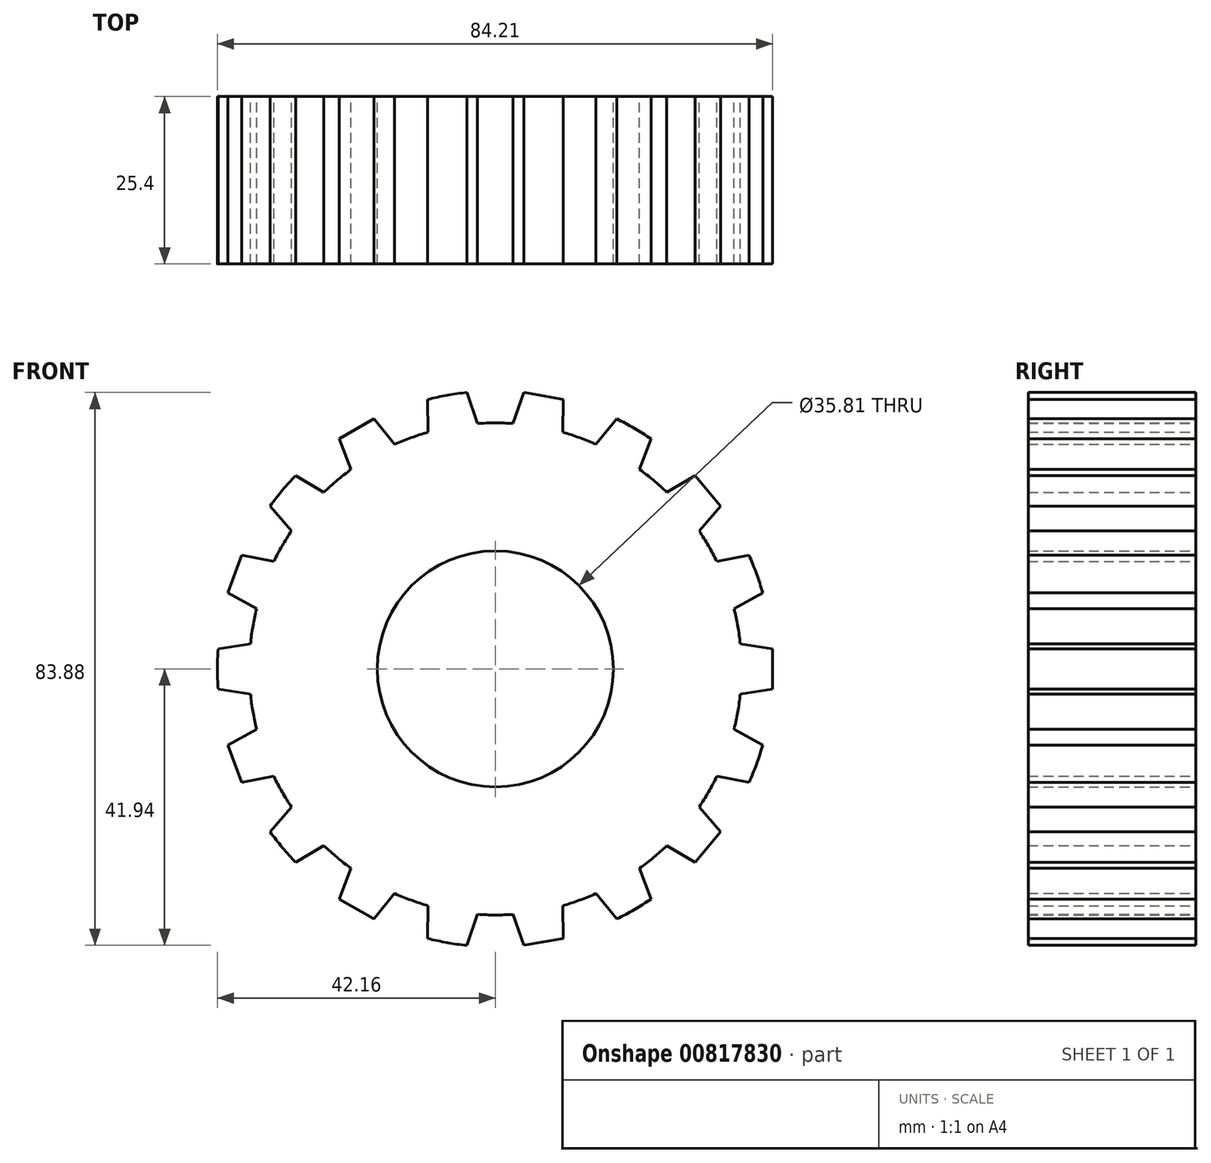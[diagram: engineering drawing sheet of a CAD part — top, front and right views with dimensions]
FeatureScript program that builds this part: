
annotation { "Feature Type Name" : "Feature", "Feature Type Description" : "" }
export const myFeature = defineFeature(function(context is Context, id is Id, definition is map)
    precondition{}
    {
        {
            var Q0;
            Q0=qCreatedBy(makeId("Front.planeOp"),FACE);
            var sketch = newSketch(context, id + "F0", { "sketchPlane" : qUnion([Q0])});
            skCircle(sketch, "E0", {"center": v(0, 0) * mm, "radius": 17.9 * mm});
            skArc(sketch, "E1", {"start": v(37.14, 3.81) * mm, "mid": v(36.77, 6.48) * mm, "end": v(36.2, 9.12) * mm});
            skArc(sketch, "E2", {"start": v(40.56, 11.53) * mm, "mid": v(39.62, 14.42) * mm, "end": v(38.48, 17.24) * mm});
            skLineSegment(sketch, "E3", {"start": v(42.16, 0) * mm, "end": v(61.21, 0) * mm});
            skLineSegment(sketch, "E4", {"start": v(42.05, 3.03) * mm, "end": v(37.14, 3.81) * mm});
            skLineSegment(sketch, "E5", {"start": v(42.05, -3.03) * mm, "end": v(37.14, -3.81) * mm});
            skLineSegment(sketch, "E6", {"start": v(42.05, 3.03) * mm, "end": v(42.05, -3.03) * mm});
            skLineSegment(sketch, "E7", {"start": v(36.2, 9.12) * mm, "end": v(40.56, 11.53) * mm});
            skLineSegment(sketch, "E8.MirrorCS", {"start": v(42.05, -3.03) * mm, "end": v(42.05, 3.03) * mm});
            skArc(sketch, "E9.MirrorCS", {"start": v(37.14, -3.81) * mm, "mid": v(36.77, -6.48) * mm, "end": v(36.2, -9.12) * mm});
            skLineSegment(sketch, "E10.MirrorCS", {"start": v(36.2, -9.12) * mm, "end": v(40.56, -11.53) * mm});
            skLineSegment(sketch, "E11.1.0", {"start": v(21.87, 30.26) * mm, "end": v(23.66, 34.9) * mm});
            skArc(sketch, "E11.1.1", {"start": v(26, 26.8) * mm, "mid": v(24, 28.6) * mm, "end": v(21.87, 30.26) * mm});
            skLineSegment(sketch, "E11.1.2", {"start": v(30.27, 29.36) * mm, "end": v(26, 26.8) * mm});
            skLineSegment(sketch, "E11.1.3", {"start": v(34.17, 24.7) * mm, "end": v(30.27, 29.36) * mm});
            skLineSegment(sketch, "E11.1.4", {"start": v(34.17, 24.7) * mm, "end": v(30.9, 20.95) * mm});
            skArc(sketch, "E11.1.5", {"start": v(30.9, 20.95) * mm, "mid": v(32.34, 18.67) * mm, "end": v(33.6, 16.29) * mm});
            skLineSegment(sketch, "E11.1.6", {"start": v(33.6, 16.29) * mm, "end": v(38.48, 17.24) * mm});
            skLineSegment(sketch, "E11.2.0", {"start": v(-2.7, 37.24) * mm, "end": v(-4.31, 41.94) * mm});
            skArc(sketch, "E11.2.1", {"start": v(2.7, 37.24) * mm, "mid": v(0, 37.34) * mm, "end": v(-2.7, 37.24) * mm});
            skLineSegment(sketch, "E11.2.2", {"start": v(4.31, 41.94) * mm, "end": v(2.7, 37.24) * mm});
            skLineSegment(sketch, "E11.2.3", {"start": v(10.3, 40.89) * mm, "end": v(4.31, 41.94) * mm});
            skLineSegment(sketch, "E11.2.4", {"start": v(10.3, 40.89) * mm, "end": v(10.2, 35.92) * mm});
            skArc(sketch, "E11.2.5", {"start": v(10.2, 35.92) * mm, "mid": v(12.77, 35.09) * mm, "end": v(15.27, 34.07) * mm});
            skLineSegment(sketch, "E11.2.6", {"start": v(15.27, 34.07) * mm, "end": v(18.4, 37.94) * mm});
            skLineSegment(sketch, "E11.3.0", {"start": v(-26, 26.8) * mm, "end": v(-30.27, 29.36) * mm});
            skArc(sketch, "E11.3.1", {"start": v(-21.87, 30.26) * mm, "mid": v(-24, 28.6) * mm, "end": v(-26, 26.8) * mm});
            skLineSegment(sketch, "E11.3.2", {"start": v(-23.66, 34.9) * mm, "end": v(-21.87, 30.26) * mm});
            skLineSegment(sketch, "E11.3.3", {"start": v(-18.4, 37.94) * mm, "end": v(-23.66, 34.9) * mm});
            skLineSegment(sketch, "E11.3.4", {"start": v(-18.4, 37.94) * mm, "end": v(-15.27, 34.07) * mm});
            skArc(sketch, "E11.3.5", {"start": v(-15.27, 34.07) * mm, "mid": v(-12.77, 35.09) * mm, "end": v(-10.2, 35.92) * mm});
            skLineSegment(sketch, "E11.3.6", {"start": v(-10.2, 35.92) * mm, "end": v(-10.3, 40.89) * mm});
            skLineSegment(sketch, "E11.4.0", {"start": v(-37.14, 3.81) * mm, "end": v(-42.05, 3.03) * mm});
            skArc(sketch, "E11.4.1", {"start": v(-36.2, 9.12) * mm, "mid": v(-36.77, 6.48) * mm, "end": v(-37.14, 3.81) * mm});
            skLineSegment(sketch, "E11.4.2", {"start": v(-40.56, 11.53) * mm, "end": v(-36.2, 9.12) * mm});
            skLineSegment(sketch, "E11.4.3", {"start": v(-38.48, 17.24) * mm, "end": v(-40.56, 11.53) * mm});
            skLineSegment(sketch, "E11.4.4", {"start": v(-38.48, 17.24) * mm, "end": v(-33.6, 16.29) * mm});
            skArc(sketch, "E11.4.5", {"start": v(-33.6, 16.29) * mm, "mid": v(-32.34, 18.67) * mm, "end": v(-30.9, 20.95) * mm});
            skLineSegment(sketch, "E11.4.6", {"start": v(-30.9, 20.95) * mm, "end": v(-34.17, 24.7) * mm});
            skLineSegment(sketch, "E11.5.0", {"start": v(-30.9, -20.95) * mm, "end": v(-34.17, -24.7) * mm});
            skArc(sketch, "E11.5.1", {"start": v(-33.6, -16.29) * mm, "mid": v(-32.34, -18.67) * mm, "end": v(-30.9, -20.95) * mm});
            skLineSegment(sketch, "E11.5.2", {"start": v(-38.48, -17.24) * mm, "end": v(-33.6, -16.29) * mm});
            skLineSegment(sketch, "E11.5.3", {"start": v(-40.56, -11.53) * mm, "end": v(-38.48, -17.24) * mm});
            skLineSegment(sketch, "E11.5.4", {"start": v(-40.56, -11.53) * mm, "end": v(-36.2, -9.12) * mm});
            skArc(sketch, "E11.5.5", {"start": v(-36.2, -9.12) * mm, "mid": v(-36.77, -6.48) * mm, "end": v(-37.14, -3.81) * mm});
            skLineSegment(sketch, "E11.5.6", {"start": v(-37.14, -3.81) * mm, "end": v(-42.05, -3.03) * mm});
            skLineSegment(sketch, "E11.6.0", {"start": v(-10.2, -35.92) * mm, "end": v(-10.3, -40.89) * mm});
            skArc(sketch, "E11.6.1", {"start": v(-15.27, -34.07) * mm, "mid": v(-12.77, -35.09) * mm, "end": v(-10.2, -35.92) * mm});
            skLineSegment(sketch, "E11.6.2", {"start": v(-18.4, -37.94) * mm, "end": v(-15.27, -34.07) * mm});
            skLineSegment(sketch, "E11.6.3", {"start": v(-23.66, -34.9) * mm, "end": v(-18.4, -37.94) * mm});
            skLineSegment(sketch, "E11.6.4", {"start": v(-23.66, -34.9) * mm, "end": v(-21.87, -30.26) * mm});
            skArc(sketch, "E11.6.5", {"start": v(-21.87, -30.26) * mm, "mid": v(-24, -28.6) * mm, "end": v(-26, -26.8) * mm});
            skLineSegment(sketch, "E11.6.6", {"start": v(-26, -26.8) * mm, "end": v(-30.27, -29.36) * mm});
            skLineSegment(sketch, "E11.7.0", {"start": v(15.27, -34.07) * mm, "end": v(18.4, -37.94) * mm});
            skArc(sketch, "E11.7.1", {"start": v(10.2, -35.92) * mm, "mid": v(12.77, -35.09) * mm, "end": v(15.27, -34.07) * mm});
            skLineSegment(sketch, "E11.7.2", {"start": v(10.3, -40.89) * mm, "end": v(10.2, -35.92) * mm});
            skLineSegment(sketch, "E11.7.3", {"start": v(4.31, -41.94) * mm, "end": v(10.3, -40.89) * mm});
            skLineSegment(sketch, "E11.7.4", {"start": v(4.31, -41.94) * mm, "end": v(2.7, -37.24) * mm});
            skArc(sketch, "E11.7.5", {"start": v(2.7, -37.24) * mm, "mid": v(0, -37.34) * mm, "end": v(-2.7, -37.24) * mm});
            skLineSegment(sketch, "E11.7.6", {"start": v(-2.7, -37.24) * mm, "end": v(-4.31, -41.94) * mm});
            skLineSegment(sketch, "E11.8.0", {"start": v(33.6, -16.29) * mm, "end": v(38.48, -17.24) * mm});
            skArc(sketch, "E11.8.1", {"start": v(30.9, -20.95) * mm, "mid": v(32.34, -18.67) * mm, "end": v(33.6, -16.29) * mm});
            skLineSegment(sketch, "E11.8.2", {"start": v(34.17, -24.7) * mm, "end": v(30.9, -20.95) * mm});
            skLineSegment(sketch, "E11.8.3", {"start": v(30.27, -29.36) * mm, "end": v(34.17, -24.7) * mm});
            skLineSegment(sketch, "E11.8.4", {"start": v(30.27, -29.36) * mm, "end": v(26, -26.8) * mm});
            skArc(sketch, "E11.8.5", {"start": v(26, -26.8) * mm, "mid": v(24, -28.6) * mm, "end": v(21.87, -30.26) * mm});
            skLineSegment(sketch, "E11.8.6", {"start": v(21.87, -30.26) * mm, "end": v(23.66, -34.9) * mm});
            skArc(sketch, "E12.trimOffspring", {"start": v(34.17, 24.7) * mm, "mid": v(32.3, 27.1) * mm, "end": v(30.27, 29.36) * mm});
            skArc(sketch, "E13.trimOffspring", {"start": v(23.66, 34.9) * mm, "mid": v(21.08, 36.52) * mm, "end": v(18.4, 37.94) * mm});
            skArc(sketch, "E14.trimOffspring", {"start": v(10.3, 40.89) * mm, "mid": v(7.32, 41.52) * mm, "end": v(4.31, 41.94) * mm});
            skArc(sketch, "E15.trimOffspring", {"start": v(-4.31, 41.94) * mm, "mid": v(-7.32, 41.52) * mm, "end": v(-10.3, 40.89) * mm});
            skArc(sketch, "E16.trimOffspring", {"start": v(-18.4, 37.94) * mm, "mid": v(-21.08, 36.52) * mm, "end": v(-23.66, 34.9) * mm});
            skArc(sketch, "E17.trimOffspring", {"start": v(-30.27, 29.36) * mm, "mid": v(-32.3, 27.1) * mm, "end": v(-34.17, 24.7) * mm});
            skArc(sketch, "E18.trimOffspring", {"start": v(-38.48, 17.24) * mm, "mid": v(-39.62, 14.42) * mm, "end": v(-40.56, 11.53) * mm});
            skArc(sketch, "E19.trimOffspring", {"start": v(-42.05, 3.03) * mm, "mid": v(-42.16, 0) * mm, "end": v(-42.05, -3.03) * mm});
            skArc(sketch, "E20.trimOffspring", {"start": v(-40.56, -11.53) * mm, "mid": v(-39.62, -14.42) * mm, "end": v(-38.48, -17.24) * mm});
            skArc(sketch, "E21.trimOffspring", {"start": v(-34.17, -24.7) * mm, "mid": v(-32.3, -27.1) * mm, "end": v(-30.27, -29.36) * mm});
            skArc(sketch, "E22.trimOffspring", {"start": v(-23.66, -34.9) * mm, "mid": v(-21.08, -36.52) * mm, "end": v(-18.4, -37.94) * mm});
            skArc(sketch, "E23.trimOffspring", {"start": v(-10.3, -40.89) * mm, "mid": v(-7.32, -41.52) * mm, "end": v(-4.31, -41.94) * mm});
            skArc(sketch, "E24.trimOffspring", {"start": v(4.31, -41.94) * mm, "mid": v(7.32, -41.52) * mm, "end": v(10.3, -40.89) * mm});
            skArc(sketch, "E25.trimOffspring", {"start": v(18.4, -37.94) * mm, "mid": v(21.08, -36.52) * mm, "end": v(23.66, -34.9) * mm});
            skArc(sketch, "E26.trimOffspring", {"start": v(30.27, -29.36) * mm, "mid": v(32.3, -27.1) * mm, "end": v(34.17, -24.7) * mm});
            skArc(sketch, "E27.trimOffspring", {"start": v(38.48, -17.24) * mm, "mid": v(39.62, -14.42) * mm, "end": v(40.56, -11.53) * mm});
            skSolve(sketch);
        }
        {
            var Q0;
            Q0=makeQuery(id+"F0.imprint","IMPRINT",FACE,{"disambiguationData":[TD([[makeQuery(id+"F0.imprint","IMPRINT",EDGE,{"derivedFrom":sQuery(id+"F0.wireOp",EDGE,"E0")}),-1.0]])]});
            extrude(context, id + "F1", {"entities" : qUnion([Q0]), "depth" : 25.4 * mm, "offsetDistance" : 25.4 * mm});
        }
    });
